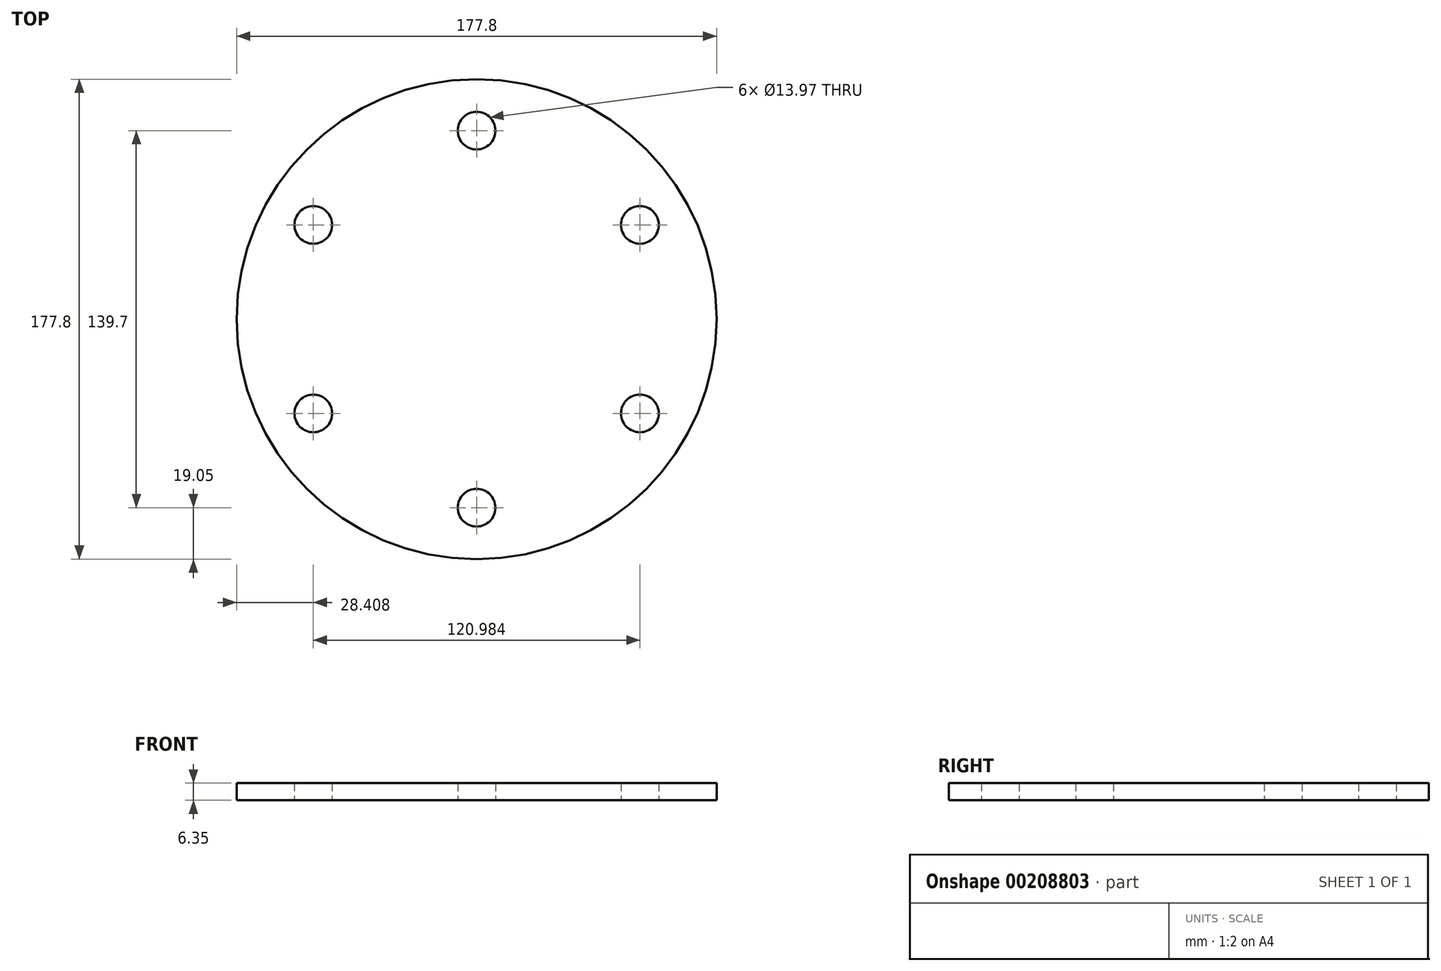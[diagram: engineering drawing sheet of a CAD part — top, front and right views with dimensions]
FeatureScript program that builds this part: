
annotation { "Feature Type Name" : "Feature", "Feature Type Description" : "" }
export const myFeature = defineFeature(function(context is Context, id is Id, definition is map)
    precondition{}
    {
        {
            var Q0;
            Q0=qCreatedBy(makeId("Top.planeOp"),FACE);
            var sketch = newSketch(context, id + "F0", { "sketchPlane" : qUnion([Q0])});
            skCircle(sketch, "E0", {"center": v(0, 0) * mm, "radius": 88.9 * mm});
            skCircle(sketch, "E1", {"center": v(0, 69.85) * mm, "radius": 6.99 * mm});
            skCircle(sketch, "E2", {"center": v(0, -69.85) * mm, "radius": 6.99 * mm});
            skCircle(sketch, "E3", {"center": v(60.5, 34.93) * mm, "radius": 6.99 * mm});
            skCircle(sketch, "E4", {"center": v(60.5, -34.93) * mm, "radius": 6.99 * mm});
            skCircle(sketch, "E5", {"center": v(-60.5, -34.93) * mm, "radius": 6.99 * mm});
            skCircle(sketch, "E6", {"center": v(-60.5, 34.93) * mm, "radius": 6.99 * mm});
            skSolve(sketch);
        }
        {
            var Q0;
            Q0 = qSketchRegion(id + "F0", true);
            extrude(context, id + "F1", {"entities" : qUnion([Q0]), "depth" : 6.35 * mm});
        }
    });
